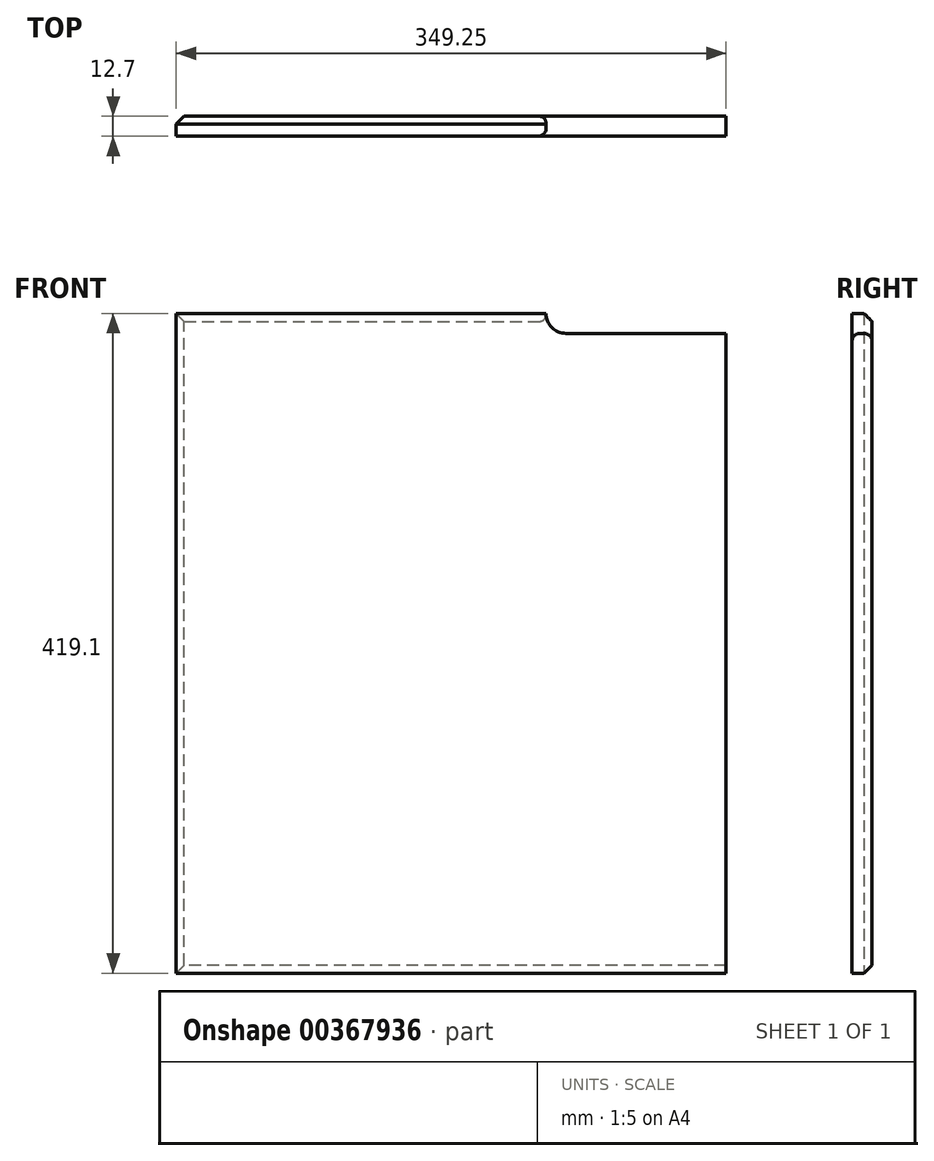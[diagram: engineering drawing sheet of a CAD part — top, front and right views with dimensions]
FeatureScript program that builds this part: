
annotation { "Feature Type Name" : "Feature", "Feature Type Description" : "" }
export const myFeature = defineFeature(function(context is Context, id is Id, definition is map)
    precondition{}
    {
        {
            var Q0;
            Q0=qCreatedBy(makeId("Front.planeOp"),FACE);
            var sketch = newSketch(context, id + "F0", { "sketchPlane" : qUnion([Q0])});
            skLineSegment(sketch, "E0.bottom", {"start": v(-179.4, 244.25) * mm, "end": v(169.86, 244.25) * mm});
            skLineSegment(sketch, "E0.top", {"start": v(-179.4, -174.85) * mm, "end": v(169.86, -174.85) * mm});
            skLineSegment(sketch, "E0.left", {"start": v(-179.4, 244.25) * mm, "end": v(-179.4, -174.85) * mm});
            skLineSegment(sketch, "E0.right", {"start": v(169.86, 244.25) * mm, "end": v(169.86, -174.85) * mm});
            skLineSegment(sketch, "E1", {"start": v(169.86, 244.25) * mm, "end": v(68.26, 244.25) * mm});
            skArc(sketch, "E2.0.endCap", {"start": v(68.26, 231.55) * mm, "mid": v(59.28, 235.26) * mm, "end": v(55.56, 244.25) * mm});
            skLineSegment(sketch, "E2.0.left", {"start": v(169.86, 231.55) * mm, "end": v(68.26, 231.55) * mm});
            skSolve(sketch);
        }
        {
            var Q0;
            {var subQ1=sQuery(id+"F0.wireOp",EDGE,"E0.top");Q0=makeQuery(id+"F0.imprint","IMPRINT",FACE,{"disambiguationData":[TD([[makeQuery(id+"F0.imprint","IMPRINT",EDGE,{"derivedFrom":subQ1}),1.0]])]});}
            extrude(context, id + "F1", {"entities" : qUnion([Q0]), "depth" : 12.7 * mm});
        }
        {
            var Q0;
            Q0=makeQuery(id+"F1.opExtrude","CAP_EDGE",EDGE,{"disambiguationData":[OSD([sQuery(id+"F0.wireOp",EDGE,"E2.0.left")])],"isStart":true});
            var Q1;
            Q1=makeQuery(id+"F1.opExtrude","CAP_EDGE",EDGE,{"disambiguationData":[OSD([sQuery(id+"F0.wireOp",EDGE,"E2.0.left")])],"isStart":false});
            fillet(context, id + "F2", {"entities" : qUnion([Q0, Q1]), "radius" : 5.08 * mm, "tangentPropagation" : true, "allowEdgeOverflow" : false});
        }
        {
            var Q0;
            Q0=makeQuery(id+"F1.opExtrude","CAP_EDGE",EDGE,{"disambiguationData":[OSD([sQuery(id+"F0.wireOp",EDGE,"E0.bottom")])],"isStart":true});
            var Q1;
            Q1=makeQuery(id+"F1.opExtrude","CAP_EDGE",EDGE,{"disambiguationData":[OSD([sQuery(id+"F0.wireOp",EDGE,"E0.left")])],"isStart":true});
            var Q2;
            Q2=makeQuery(id+"F1.opExtrude","CAP_EDGE",EDGE,{"disambiguationData":[OSD([sQuery(id+"F0.wireOp",EDGE,"E0.top")])],"isStart":true});
            chamfer(context, id + "F3", {"entities" : qUnion([Q0, Q1, Q2]), "width" : 5.08 * mm});
        }
    });
